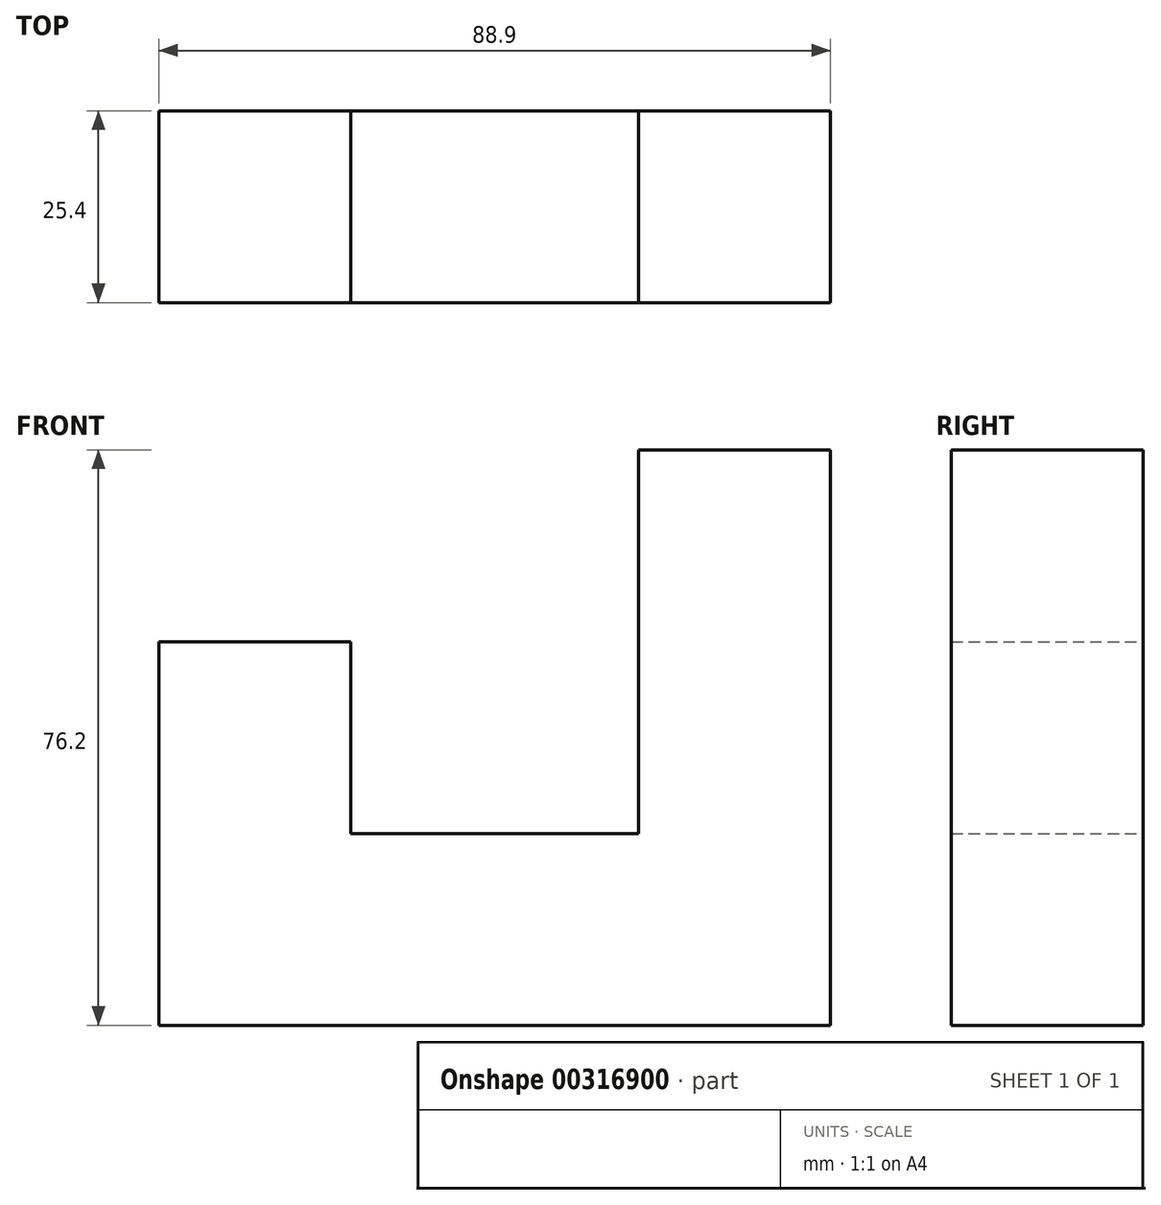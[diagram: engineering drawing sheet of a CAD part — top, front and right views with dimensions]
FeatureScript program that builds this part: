
annotation { "Feature Type Name" : "Feature", "Feature Type Description" : "" }
export const myFeature = defineFeature(function(context is Context, id is Id, definition is map)
    precondition{}
    {
        {
            var Q0;
            Q0=qCreatedBy(makeId("Front.planeOp"),FACE);
            var sketch = newSketch(context, id + "F0", { "sketchPlane" : qUnion([Q0])});
            skLineSegment(sketch, "E0", {"start": v(-38.03, 17.73) * mm, "end": v(-63.43, 17.73) * mm});
            skLineSegment(sketch, "E1", {"start": v(-63.43, 17.73) * mm, "end": v(-63.43, -33.07) * mm});
            skLineSegment(sketch, "E2", {"start": v(-63.43, -33.07) * mm, "end": v(25.47, -33.07) * mm});
            skLineSegment(sketch, "E3", {"start": v(25.47, -33.07) * mm, "end": v(25.47, 43.13) * mm});
            skLineSegment(sketch, "E4", {"start": v(25.47, 43.13) * mm, "end": v(0.07, 43.13) * mm});
            skLineSegment(sketch, "E5", {"start": v(0.07, 43.13) * mm, "end": v(0.07, -7.67) * mm});
            skLineSegment(sketch, "E6", {"start": v(0.07, -7.67) * mm, "end": v(-38.03, -7.67) * mm});
            skLineSegment(sketch, "E7", {"start": v(-38.03, -7.67) * mm, "end": v(-38.03, 17.73) * mm});
            skSolve(sketch);
        }
        {
            var Q0;
            Q0=makeQuery(id+"F0.imprint","IMPRINT",FACE,{"disambiguationData":[TD([[makeQuery(id+"F0.imprint","IMPRINT",EDGE,{"derivedFrom":sQuery(id+"F0.wireOp",EDGE,"E0")}),1.0]])]});
            extrude(context, id + "F1", {"entities" : qUnion([Q0]), "depth" : 25.4 * mm});
        }
    });
